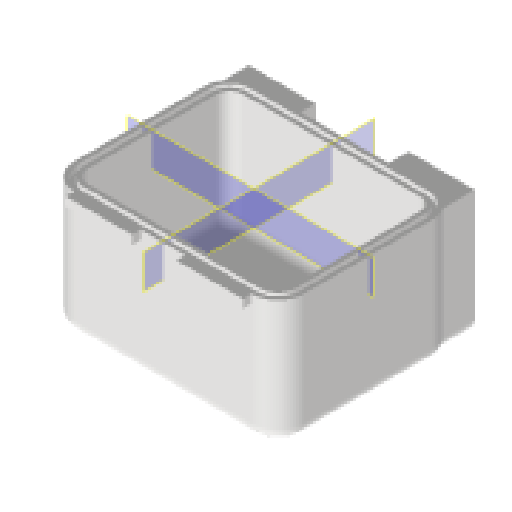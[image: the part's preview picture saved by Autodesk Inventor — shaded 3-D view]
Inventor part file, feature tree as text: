
AUTODESK INVENTOR PART (.ipt)
format: ipt  version: 2024.1 (Build 281209000, 209)  size: 2,390,016 bytes
history: native  units: mm
features: extrude x6, sketch x6, projected_geometry x5, plane x2, fillet x1, other x1
ambient origin geometry x8: Origin, YZ Plane, XZ Plane, XY Plane, X Axis, Y Axis, Z Axis, Center Point
bodies: Volumenkörper1 (feature_tree)
feature tree (21):
  extrude  "Extrusion1"  Depth=178.0mm
  extrude  "Extrusion2"  Depth=15.0mm
  fillet  "Rundung1"  Radius=137.0mm
  extrude  "Extrusion3"  Depth=15.0mm
  extrude  "Extrusion4"  Depth=5.0mm
  plane  "Arbeitsebene1"
  plane  "Arbeitsebene2"
  extrude  "Extrusion5"  Depth=5.0mm
  extrude  "Extrusion6"  Depth=76.0mm
  sketch  "Skizze1"  dims[d10=233.0mm d11=178.0mm]
  other  "Bild1"
  sketch  "Skizze2"  dims[d13=15.0mm d14=15.0mm d15=137.0mm d16=0.0mm]
  projected_geometry  "Projizierte Kontur1"
  sketch  "Skizze3"  dims[d17=6.0mm d18=0.0mm d19=15.0mm]
  projected_geometry  "Projizierte Kontur2"
  sketch  "Skizze4"  dims[d20=5.0mm d21=5.0mm]
  projected_geometry  "Projizierte Kontur3"
  sketch  "Skizze5"  dims[d22=6.0mm d23=0.0mm d24=5.0mm]
  projected_geometry  "Projizierte Kontur4"
  sketch  "Skizze6"  dims[d25=17.0mm d26=76.0mm d27=5.0mm d28=76.0mm d30=76.0mm d31=10.0mm d32=76.0mm d33=10.0mm d34=0.0mm d36=22.0mm d37=22.0mm d38=22.0mm d39=22.0mm d40=0.0mm d41=3.0mm d42=0.0mm d43=0.0mm]
  projected_geometry  "Projizierte Kontur5"
